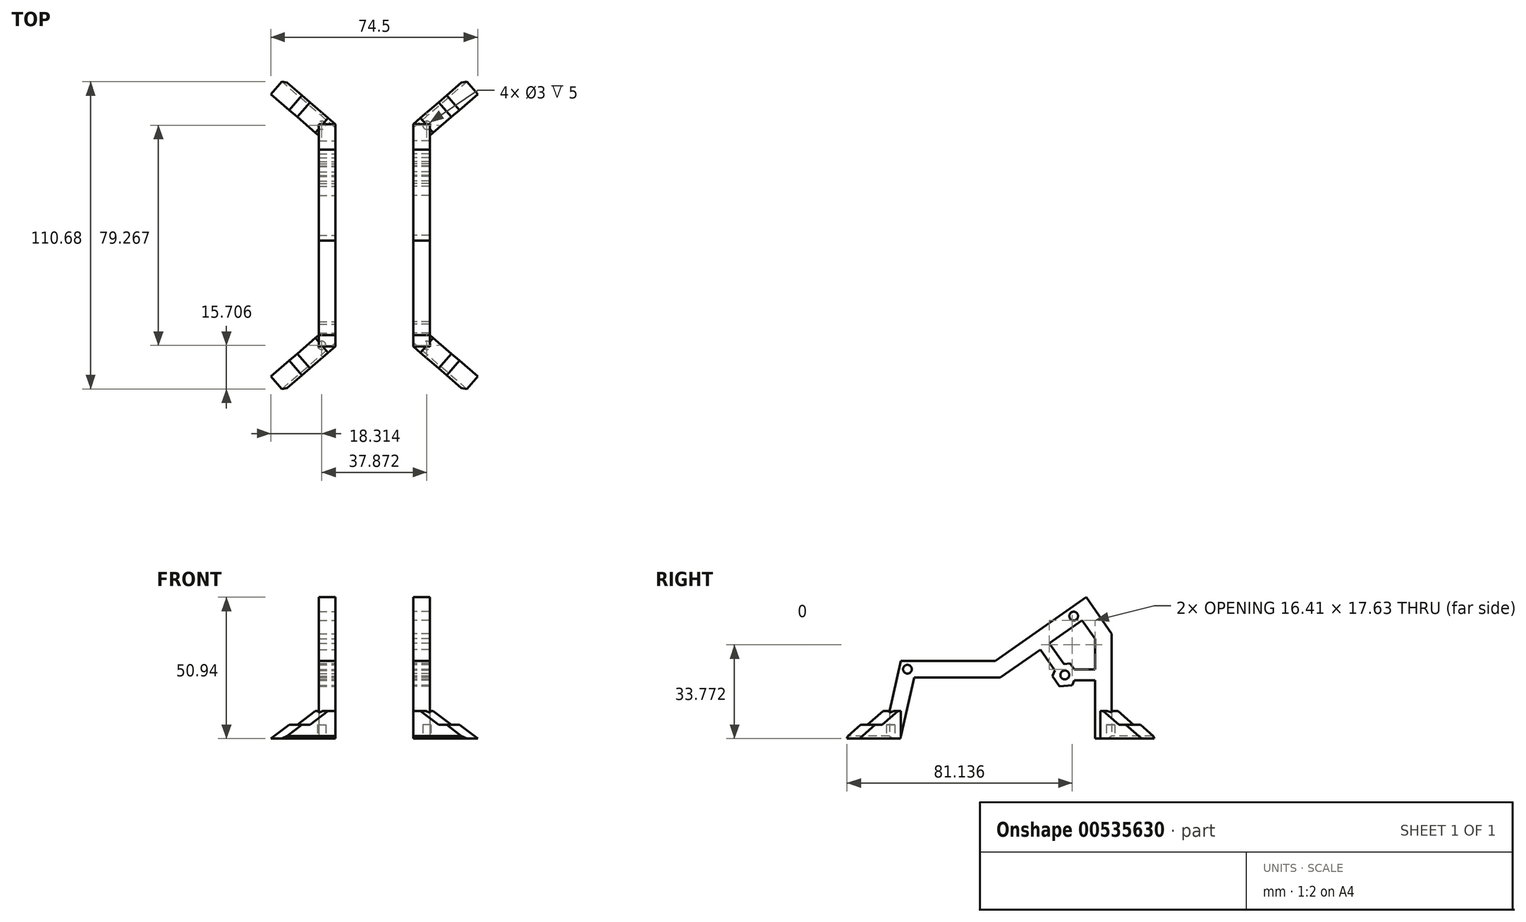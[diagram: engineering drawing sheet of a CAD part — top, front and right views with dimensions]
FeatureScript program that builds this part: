
annotation { "Feature Type Name" : "Feature", "Feature Type Description" : "" }
export const myFeature = defineFeature(function(context is Context, id is Id, definition is map)
    precondition{}
    {
        {
            var Q0;
            Q0=qCreatedBy(makeId("Top.planeOp"),FACE);
            var sketch = newSketch(context, id + "F0", { "sketchPlane" : qUnion([Q0])});
            skLineSegment(sketch, "E0", {"start": v(14, 40) * mm, "end": v(32.94, 56.32) * mm});
            skLineSegment(sketch, "E1", {"start": v(32.94, 56.32) * mm, "end": v(37.5, 51.02) * mm});
            skLineSegment(sketch, "E2", {"start": v(37.5, 51.02) * mm, "end": v(18.57, 34.7) * mm});
            skLineSegment(sketch, "E3", {"start": v(14, 40) * mm, "end": v(0, 40) * mm, "construction": true});
            skLineSegment(sketch, "E4", {"start": v(0, 40) * mm, "end": v(0, 0) * mm, "construction": true});
            skLineSegment(sketch, "E5", {"start": v(14, 40) * mm, "end": v(18.57, 34.7) * mm});
            skCircle(sketch, "E6", {"center": v(18.94, 39.63) * mm, "radius": 1.5 * mm});
            skLineSegment(sketch, "E7", {"start": v(14, 40) * mm, "end": v(20, 40) * mm});
            skLineSegment(sketch, "E8", {"start": v(20, 40) * mm, "end": v(20, 0) * mm});
            skLineSegment(sketch, "E9", {"start": v(14, 40) * mm, "end": v(14, 0) * mm});
            skLineSegment(sketch, "E10", {"start": v(23.47, 48.16) * mm, "end": v(28.04, 42.86) * mm});
            skLineSegment(sketch, "E11.MirrorCS", {"start": v(23.47, -48.16) * mm, "end": v(28.04, -42.86) * mm});
            skLineSegment(sketch, "E12.MirrorCS", {"start": v(14, -40) * mm, "end": v(20, -40) * mm});
            skCircle(sketch, "E13.MirrorC", {"center": v(18.94, -39.63) * mm, "radius": 1.5 * mm});
            skLineSegment(sketch, "E14.MirrorCS", {"start": v(14, -40) * mm, "end": v(18.57, -34.7) * mm});
            skLineSegment(sketch, "E15.MirrorCS", {"start": v(14, -40) * mm, "end": v(14, 0) * mm});
            skLineSegment(sketch, "E16.MirrorCS", {"start": v(20, -40) * mm, "end": v(20, 0) * mm});
            skLineSegment(sketch, "E17.MirrorCS", {"start": v(14, -40) * mm, "end": v(0, -40) * mm, "construction": true});
            skLineSegment(sketch, "E18.MirrorCS", {"start": v(0, -40) * mm, "end": v(0, 0) * mm, "construction": true});
            skLineSegment(sketch, "E19.MirrorCS", {"start": v(37.5, -51.02) * mm, "end": v(18.57, -34.7) * mm});
            skLineSegment(sketch, "E20.MirrorCS", {"start": v(32.94, -56.32) * mm, "end": v(37.5, -51.02) * mm});
            skLineSegment(sketch, "E21.MirrorCS", {"start": v(14, -40) * mm, "end": v(32.94, -56.32) * mm});
            skSolve(sketch);
        }
        {
            var Q0;
            {var subQ1=sQuery(id+"F0.wireOp",EDGE,"E5");Q0=makeQuery(id+"F0.imprint","IMPRINT",FACE,{"disambiguationData":[TD([[makeQuery(id+"F0.imprint","IMPRINT",EDGE,{"derivedFrom":subQ1}),1.0]])]});}
            var Q1;
            {var subQ0=sQuery(id+"F0.wireOp",EDGE,"E7");var subQ1=sQuery(id+"F0.wireOp",EDGE,"E6");var subQ2=makeQuery(id+"F0.imprint","INTERSECT",VERTEX,{"derivedFrom":[subQ1,subQ0]});Q1=makeQuery(id+"F0.imprint","IMPRINT",FACE,{"disambiguationData":[TD([[makeQuery(id+"F0.imprint","IMPRINT",EDGE,{"disambiguationData":[TD([[subQ2,-1.0]])],"derivedFrom":subQ1}),1.0]])]});}
            var Q2;
            {var subQ7=sQuery(id+"F0.wireOp",EDGE,"E5");Q2=makeQuery(id+"F0.imprint","IMPRINT",FACE,{"disambiguationData":[TD([[makeQuery(id+"F0.imprint","IMPRINT",EDGE,{"derivedFrom":subQ7}),-1.0]])]});}
            var Q3;
            {var subQ0=sQuery(id+"F0.wireOp",EDGE,"E14.MirrorCS");Q3=makeQuery(id+"F0.imprint","IMPRINT",FACE,{"disambiguationData":[TD([[makeQuery(id+"F0.imprint","IMPRINT",EDGE,{"derivedFrom":subQ0}),-1.0]])]});}
            var Q4;
            {var subQ0=sQuery(id+"F0.wireOp",EDGE,"E16.MirrorCS");var subQ1=sQuery(id+"F0.wireOp",EDGE,"E12.MirrorCS");var subQ2=makeQuery(id+"F0.imprint","INTERSECT",VERTEX,{"derivedFrom":[subQ1,subQ0]});Q4=makeQuery(id+"F0.imprint","IMPRINT",FACE,{"disambiguationData":[TD([[makeQuery(id+"F0.imprint","IMPRINT",EDGE,{"disambiguationData":[TD([[subQ2,1.0]])],"derivedFrom":subQ1}),1.0]])]});}
            extrude(context, id + "F1", {"entities" : qUnion([Q0, Q1, Q2, Q3, Q4]), "depth" : 70 * mm});
        }
        {
            var Q0;
            {var subQ0=sQuery(id+"F0.wireOp",EDGE,"E7");var subQ1=sQuery(id+"F0.wireOp",EDGE,"E6");var subQ2=makeQuery(id+"F0.imprint","INTERSECT",VERTEX,{"derivedFrom":[subQ1,subQ0]});Q0=makeQuery(id+"F0.imprint","IMPRINT",FACE,{"disambiguationData":[TD([[makeQuery(id+"F0.imprint","IMPRINT",EDGE,{"disambiguationData":[TD([[subQ2,1.0]])],"derivedFrom":subQ1}),1.0]])]});}
            var Q1;
            {var subQ7=sQuery(id+"F0.wireOp",EDGE,"E10");Q1=makeQuery(id+"F0.imprint","IMPRINT",FACE,{"disambiguationData":[TD([[makeQuery(id+"F0.imprint","IMPRINT",EDGE,{"derivedFrom":subQ7}),-1.0]])]});}
            var Q2;
            {var subQ9=sQuery(id+"F0.wireOp",EDGE,"E11.MirrorCS");Q2=makeQuery(id+"F0.imprint","IMPRINT",FACE,{"disambiguationData":[TD([[makeQuery(id+"F0.imprint","IMPRINT",EDGE,{"derivedFrom":subQ9}),1.0]])]});}
            var Q3;
            {var subQ0=sQuery(id+"F0.wireOp",EDGE,"E16.MirrorCS");var subQ1=sQuery(id+"F0.wireOp",EDGE,"E12.MirrorCS");var subQ2=makeQuery(id+"F0.imprint","INTERSECT",VERTEX,{"derivedFrom":[subQ1,subQ0]});Q3=makeQuery(id+"F0.imprint","IMPRINT",FACE,{"disambiguationData":[TD([[makeQuery(id+"F0.imprint","IMPRINT",EDGE,{"disambiguationData":[TD([[subQ2,1.0]])],"derivedFrom":subQ1}),-1.0]])]});}
            extrude(context, id + "F2", {"entities" : qUnion([Q0, Q1, Q2, Q3]), "operationType" : NewBodyOperationType.ADD, "depth" : 10 * mm, "offsetDistance" : 25 * mm});
        }
        {
            var Q0;
            {var subQ0=sQuery(id+"F0.wireOp",EDGE,"E1");Q0=makeQuery(id+"F0.imprint","IMPRINT",FACE,{"disambiguationData":[TD([[makeQuery(id+"F0.imprint","IMPRINT",EDGE,{"derivedFrom":subQ0}),-1.0]])]});}
            var Q1;
            {var subQ0=sQuery(id+"F0.wireOp",EDGE,"E11.MirrorCS");Q1=makeQuery(id+"F0.imprint","IMPRINT",FACE,{"disambiguationData":[TD([[makeQuery(id+"F0.imprint","IMPRINT",EDGE,{"derivedFrom":subQ0}),-1.0]])]});}
            extrude(context, id + "F3", {"entities" : qUnion([Q0, Q1]), "operationType" : NewBodyOperationType.ADD, "depth" : 5 * mm});
        }
        {
            var Q0;
            Q0=makeQuery(id+"F1.opExtrude","SWEPT_FACE",FACE,{"disambiguationData":[OSD([sQuery(id+"F0.wireOp",EDGE,"E9"),sQuery(id+"F0.wireOp",EDGE,"E15.MirrorCS")])]});
            var sketch = newSketch(context, id + "F4", { "sketchPlane" : qUnion([Q0])});
            skLineSegment(sketch, "E22", {"start": v(0, 0) * mm, "end": v(0, 28) * mm, "construction": true});
            skPoint(sketch, "E22.endSnap0", {"position": v(0, 0) * mm});
            skLineSegment(sketch, "E23", {"start": v(-20.33, 28) * mm, "end": v(19.67, 28) * mm, "construction": true});
            skLineSegment(sketch, "E24", {"start": v(1.95, 28) * mm, "end": v(-30.81, 50.94) * mm});
            skLineSegment(sketch, "E25", {"start": v(40, 10) * mm, "end": v(35.95, 28) * mm});
            skLineSegment(sketch, "E26", {"start": v(35.95, 28) * mm, "end": v(1.95, 28) * mm});
            skLineSegment(sketch, "E27", {"start": v(-30.81, 50.94) * mm, "end": v(-40, 37.83) * mm});
            skLineSegment(sketch, "E28", {"start": v(-40, 37.83) * mm, "end": v(-40, 0) * mm});
            skLineSegment(sketch, "E29", {"start": v(36.1, 0) * mm, "end": v(31.15, 22) * mm});
            skLineSegment(sketch, "E30", {"start": v(31.15, 22) * mm, "end": v(0.06, 22) * mm});
            skLineSegment(sketch, "E31", {"start": v(0.06, 22) * mm, "end": v(-14.32, 32.07) * mm});
            skLineSegment(sketch, "E32", {"start": v(-29.34, 42.59) * mm, "end": v(-34, 35.93) * mm});
            skLineSegment(sketch, "E33", {"start": v(-34, 35.93) * mm, "end": v(-34, 24.96) * mm});
            skLineSegment(sketch, "E34", {"start": v(-14.32, 32.07) * mm, "end": v(-22.1, 20.96) * mm});
            skLineSegment(sketch, "E35", {"start": v(-22.1, 20.96) * mm, "end": v(-34, 20.96) * mm});
            skLineSegment(sketch, "E36", {"start": v(-17.6, 34.36) * mm, "end": v(-24.18, 24.96) * mm});
            skLineSegment(sketch, "E37", {"start": v(-24.18, 24.96) * mm, "end": v(-34, 24.96) * mm});
            skLineSegment(sketch, "E38", {"start": v(-24.18, 24.96) * mm, "end": v(-22.1, 20.96) * mm, "construction": true});
            skCircle(sketch, "E39", {"center": v(-23.13, 22.96) * mm, "radius": 1.6 * mm});
            skLineSegment(sketch, "E40.trimOffspring", {"start": v(-17.6, 34.36) * mm, "end": v(-29.34, 42.59) * mm});
            skLineSegment(sketch, "E41.trimOffspring", {"start": v(-34, 20.96) * mm, "end": v(-34, 0) * mm});
            skLineSegment(sketch, "E42", {"start": v(-24.62, 46.6) * mm, "end": v(-26.34, 44.15) * mm, "construction": true});
            skCircle(sketch, "E43", {"center": v(-26.34, 44.15) * mm, "radius": 1.57 * mm});
            skLineSegment(sketch, "E44", {"start": v(35.95, 28) * mm, "end": v(31.15, 22) * mm, "construction": true});
            skCircle(sketch, "E45", {"center": v(33.55, 25) * mm, "radius": 1.57 * mm});
            skCircle(sketch, "E46.cCircle", {"center": v(-23.13, 22.96) * mm, "radius": 3.92 * mm, "construction": true});
            skLineSegment(sketch, "E46.0", {"start": v(-27.65, 23.35) * mm, "end": v(-25.05, 27.06) * mm});
            skLineSegment(sketch, "E46.1", {"start": v(-25.05, 27.06) * mm, "end": v(-20.54, 26.67) * mm});
            skLineSegment(sketch, "E46.2", {"start": v(-20.54, 26.67) * mm, "end": v(-18.62, 22.56) * mm});
            skLineSegment(sketch, "E46.3", {"start": v(-18.62, 22.56) * mm, "end": v(-21.22, 18.85) * mm});
            skLineSegment(sketch, "E46.4", {"start": v(-21.22, 18.85) * mm, "end": v(-25.73, 19.25) * mm});
            skLineSegment(sketch, "E46.5", {"start": v(-25.73, 19.25) * mm, "end": v(-27.65, 23.35) * mm});
            skPoint(sketch, "E46.0.midPoint", {"position": v(-26.35, 25.2) * mm});
            skSolve(sketch);
        }
        {
            var Q0;
            {var subQ0=sQuery(id+"F4.wireOp",EDGE,"E29");Q0=makeQuery(id+"F4.imprint","IMPRINT",FACE,{"disambiguationData":[TD([[makeQuery(id+"F4.imprint","IMPRINT",EDGE,{"derivedFrom":subQ0}),1.0]])]});}
            var Q1;
            Q1=makeQuery(id+"F4.imprint","IMPRINT",FACE,{"disambiguationData":[TD([[makeQuery(id+"F4.imprint","IMPRINT",EDGE,{"derivedFrom":sQuery(id+"F4.wireOp",EDGE,"E24")}),-1.0]])]});
            var Q2;
            Q2=makeQuery(id+"F4.imprint","IMPRINT",FACE,{"disambiguationData":[TD([[makeQuery(id+"F4.imprint","IMPRINT",EDGE,{"derivedFrom":sQuery(id+"F4.wireOp",EDGE,"E32")}),1.0]])]});
            var Q3;
            Q3=makeQuery(id+"F4.imprint","IMPRINT",FACE,{"disambiguationData":[TD([[makeQuery(id+"F4.imprint","IMPRINT",EDGE,{"derivedFrom":sQuery(id+"F4.wireOp",EDGE,"E39")}),1.0]])]});
            var Q4;
            Q4=makeQuery(id+"F4.imprint","IMPRINT",FACE,{"disambiguationData":[TD([[makeQuery(id+"F4.imprint","IMPRINT",EDGE,{"derivedFrom":sQuery(id+"F4.wireOp",EDGE,"E43")}),1.0]])]});
            var Q5;
            Q5=makeQuery(id+"F4.imprint","IMPRINT",FACE,{"disambiguationData":[TD([[makeQuery(id+"F4.imprint","IMPRINT",EDGE,{"derivedFrom":sQuery(id+"F4.wireOp",EDGE,"E45")}),1.0]])]});
            extrude(context, id + "F5", {"entities" : qUnion([Q0, Q1, Q2, Q3, Q4, Q5]), "operationType" : NewBodyOperationType.REMOVE, "oppositeDirection" : true, "depth" : 25 * mm, "offsetDistance" : 25 * mm});
        }
        {
            var Q0;
            {var subQ0=sQuery(id+"F0.wireOp",EDGE,"E16.MirrorCS");var subQ1=sQuery(id+"F0.wireOp",EDGE,"E12.MirrorCS");var subQ2=makeQuery(id+"F0.imprint","INTERSECT",VERTEX,{"derivedFrom":[subQ1,subQ0]});Q0=makeQuery(id+"F0.imprint","IMPRINT",FACE,{"disambiguationData":[TD([[makeQuery(id+"F0.imprint","IMPRINT",EDGE,{"disambiguationData":[TD([[subQ2,1.0]])],"derivedFrom":subQ1}),-1.0]])]});}
            var Q1;
            {var subQ0=sQuery(id+"F0.wireOp",EDGE,"E16.MirrorCS");var subQ1=sQuery(id+"F0.wireOp",EDGE,"E12.MirrorCS");var subQ2=makeQuery(id+"F0.imprint","INTERSECT",VERTEX,{"derivedFrom":[subQ1,subQ0]});Q1=makeQuery(id+"F0.imprint","IMPRINT",FACE,{"disambiguationData":[TD([[makeQuery(id+"F0.imprint","IMPRINT",EDGE,{"disambiguationData":[TD([[subQ2,1.0]])],"derivedFrom":subQ1}),1.0]])]});}
            var Q2;
            {var subQ0=sQuery(id+"F0.wireOp",EDGE,"E7");var subQ1=sQuery(id+"F0.wireOp",EDGE,"E6");var subQ2=makeQuery(id+"F0.imprint","INTERSECT",VERTEX,{"derivedFrom":[subQ1,subQ0]});Q2=makeQuery(id+"F0.imprint","IMPRINT",FACE,{"disambiguationData":[TD([[makeQuery(id+"F0.imprint","IMPRINT",EDGE,{"disambiguationData":[TD([[subQ2,1.0]])],"derivedFrom":subQ1}),1.0]])]});}
            var Q3;
            {var subQ0=sQuery(id+"F0.wireOp",EDGE,"E7");var subQ1=sQuery(id+"F0.wireOp",EDGE,"E6");var subQ2=makeQuery(id+"F0.imprint","INTERSECT",VERTEX,{"derivedFrom":[subQ1,subQ0]});Q3=makeQuery(id+"F0.imprint","IMPRINT",FACE,{"disambiguationData":[TD([[makeQuery(id+"F0.imprint","IMPRINT",EDGE,{"disambiguationData":[TD([[subQ2,-1.0]])],"derivedFrom":subQ1}),1.0]])]});}
            extrude(context, id + "F6", {"entities" : qUnion([Q0, Q1, Q2, Q3]), "operationType" : NewBodyOperationType.REMOVE, "depth" : 5 * mm});
        }
        {
            var Q0;
            {var subQ0=sQuery(id+"F0.wireOp",EDGE,"E21.MirrorCS");Q0=makeQuery(id+"FMU3Kzz7f9KnHee_2.opPattern","COPY",EDGE,{"derivedFrom":makeQuery(id+"F3.boolean.opBoolean","MERGE",EDGE,{"derivedFrom":[makeQuery(id+"F2.opExtrude","CAP_EDGE",EDGE,{"disambiguationData":[OSD([subQ0])],"isStart":true}),makeQuery(id+"F3.opExtrude","CAP_EDGE",EDGE,{"disambiguationData":[OSD([subQ0])],"isStart":true})]}),"instanceName":"1"});}
            var Q1;
            {var subQ0=sQuery(id+"F0.wireOp",EDGE,"E21.MirrorCS");Q1=makeQuery(id+"F3.boolean.opBoolean","MERGE",EDGE,{"derivedFrom":[makeQuery(id+"F2.opExtrude","CAP_EDGE",EDGE,{"disambiguationData":[OSD([subQ0])],"isStart":true}),makeQuery(id+"F3.opExtrude","CAP_EDGE",EDGE,{"disambiguationData":[OSD([subQ0])],"isStart":true})]});}
            var Q2;
            {var subQ0=sQuery(id+"F0.wireOp",EDGE,"E0");Q2=makeQuery(id+"F3.boolean.opBoolean","MERGE",EDGE,{"derivedFrom":[makeQuery(id+"F2.opExtrude","CAP_EDGE",EDGE,{"disambiguationData":[OSD([subQ0])],"isStart":true}),makeQuery(id+"F3.opExtrude","CAP_EDGE",EDGE,{"disambiguationData":[OSD([subQ0])],"isStart":true})]});}
            var Q3;
            {var subQ0=sQuery(id+"F0.wireOp",EDGE,"E0");Q3=makeQuery(id+"FMU3Kzz7f9KnHee_2.opPattern","COPY",EDGE,{"derivedFrom":makeQuery(id+"F3.boolean.opBoolean","MERGE",EDGE,{"derivedFrom":[makeQuery(id+"F2.opExtrude","CAP_EDGE",EDGE,{"disambiguationData":[OSD([subQ0])],"isStart":true}),makeQuery(id+"F3.opExtrude","CAP_EDGE",EDGE,{"disambiguationData":[OSD([subQ0])],"isStart":true})]}),"instanceName":"1"});}
            chamfer(context, id + "F7", {"entities" : qUnion([Q0, Q1, Q2, Q3]), "width" : 1 * mm, "tangentPropagation" : true});
        }
        {
            var Q0;
            Q0=makeQuery(id+"F3.opExtrude","CAP_EDGE",EDGE,{"disambiguationData":[OSD([sQuery(id+"F0.wireOp",EDGE,"E20.MirrorCS")])],"isStart":false});
            var Q1;
            Q1=makeQuery(id+"F2.opExtrude","CAP_EDGE",EDGE,{"disambiguationData":[OSD([sQuery(id+"F0.wireOp",EDGE,"E11.MirrorCS")])],"isStart":false});
            chamfer(context, id + "F8", {"entities" : qUnion([Q0, Q1]), "chamferType" : ChamferType.OFFSET_ANGLE, "width" : 9 * mm, "oppositeDirection" : false, "angle" : 30 * degree, "tangentPropagation" : true});
        }
        {
            var Q0;
            Q0=makeQuery(id+"F3.opExtrude","CAP_EDGE",EDGE,{"disambiguationData":[OSD([sQuery(id+"F0.wireOp",EDGE,"E1")])],"isStart":false});
            var Q1;
            Q1=makeQuery(id+"F2.opExtrude","CAP_EDGE",EDGE,{"disambiguationData":[OSD([sQuery(id+"F0.wireOp",EDGE,"E10")])],"isStart":false});
            chamfer(context, id + "F9", {"entities" : qUnion([Q0, Q1]), "chamferType" : ChamferType.OFFSET_ANGLE, "width" : 9 * mm, "oppositeDirection" : true, "angle" : 30 * degree, "tangentPropagation" : true});
        }
        {
            var Q0;
            Q0=makeQuery(id+"F1.opExtrude","SWEPT_BODY",BODY,{"disambiguationData":[OSD([sQuery(id+"F0.wireOp",EDGE,"E7"),sQuery(id+"F0.wireOp",EDGE,"E8"),sQuery(id+"F0.wireOp",EDGE,"E9"),sQuery(id+"F0.wireOp",EDGE,"E12.MirrorCS"),sQuery(id+"F0.wireOp",EDGE,"E15.MirrorCS"),sQuery(id+"F0.wireOp",EDGE,"E16.MirrorCS")])]});
            var Q1;
            Q1=qCreatedBy(makeId("Right.planeOp"),FACE);
            mirror(context, id + "F10", {"entities" : qUnion([Q0]), "mirrorPlane" : qUnion([Q1])});
        }
    });
